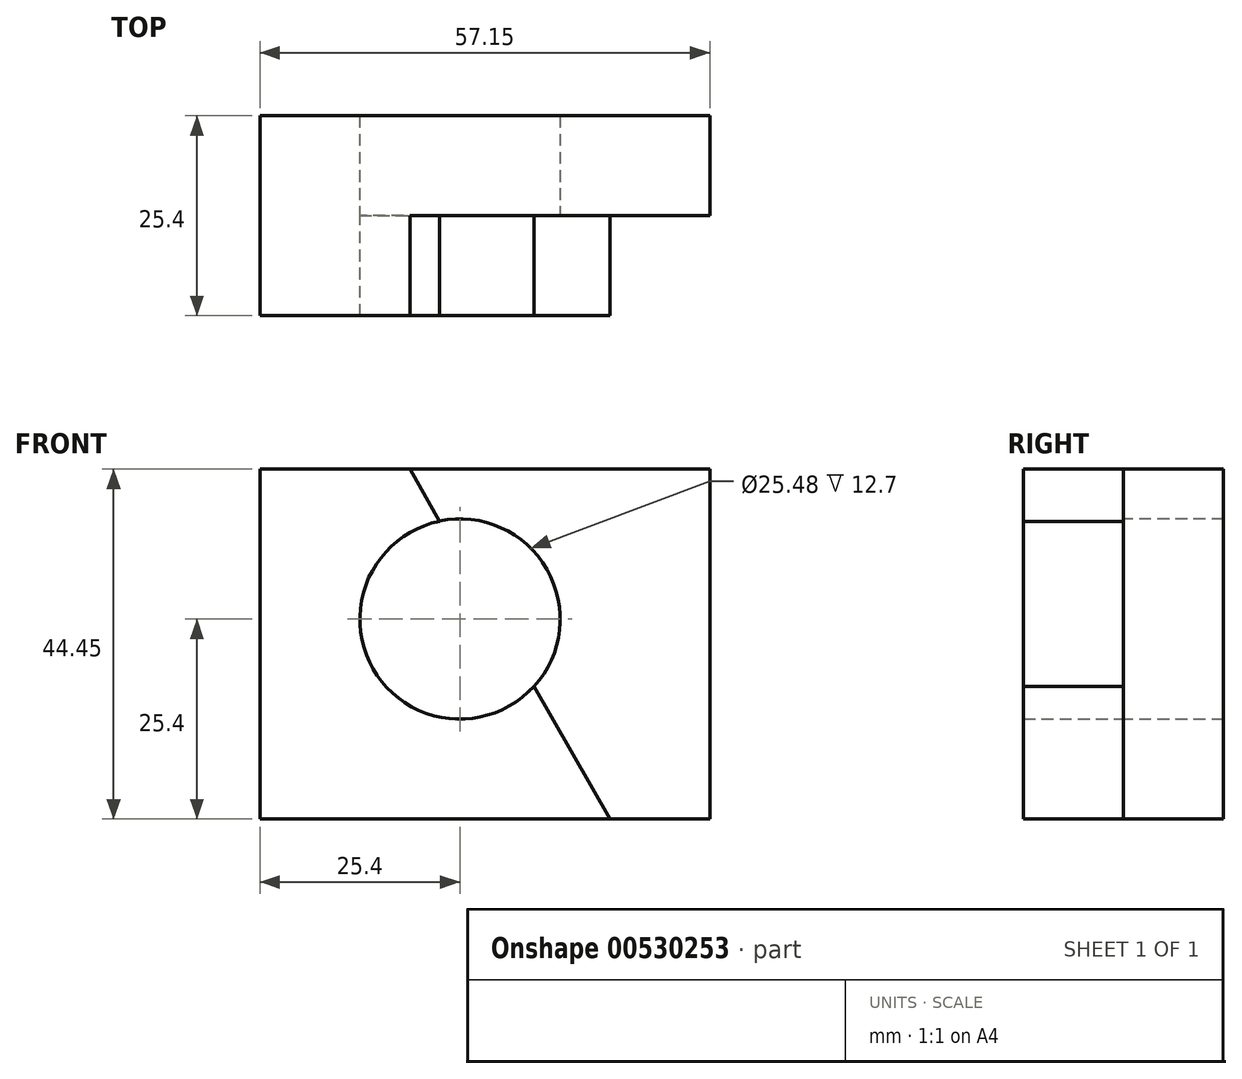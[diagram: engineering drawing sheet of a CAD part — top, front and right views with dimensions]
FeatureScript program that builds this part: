
annotation { "Feature Type Name" : "Feature", "Feature Type Description" : "" }
export const myFeature = defineFeature(function(context is Context, id is Id, definition is map)
    precondition{}
    {
        {
            var Q0;
            Q0=qCreatedBy(makeId("Front.planeOp"),FACE);
            var sketch = newSketch(context, id + "F0", { "sketchPlane" : qUnion([Q0])});
            skLineSegment(sketch, "E0.bottom", {"start": v(-57.15, 44.45) * mm, "end": v(0, 44.45) * mm});
            skLineSegment(sketch, "E0.top", {"start": v(-57.15, 0) * mm, "end": v(0, 0) * mm});
            skLineSegment(sketch, "E0.left", {"start": v(-57.15, 44.45) * mm, "end": v(-57.15, 0) * mm});
            skLineSegment(sketch, "E0.right", {"start": v(0, 44.45) * mm, "end": v(0, 0) * mm});
            skSolve(sketch);
        }
        {
            var Q0;
            Q0 = qSketchRegion(id + "F0", true);
            extrude(context, id + "F1", {"entities" : qUnion([Q0]), "depth" : 25.4 * mm, "offsetDistance" : 25.4 * mm});
        }
        {
            var Q0;
            Q0=makeQuery(id+"F1.opExtrude","CAP_FACE",FACE,{"disambiguationData":[OSD([sQuery(id+"F0.wireOp",EDGE,"E0.bottom"),sQuery(id+"F0.wireOp",EDGE,"E0.top"),sQuery(id+"F0.wireOp",EDGE,"E0.left"),sQuery(id+"F0.wireOp",EDGE,"E0.right")])],"isStart":false});
            var sketch = newSketch(context, id + "F2", { "sketchPlane" : qUnion([Q0])});
            skLineSegment(sketch, "E1", {"start": v(-38.1, 44.45) * mm, "end": v(-12.7, 0) * mm});
            skLineSegment(sketch, "E2", {"start": v(-12.7, 0) * mm, "end": v(0, 0) * mm});
            skLineSegment(sketch, "E3", {"start": v(0, 0) * mm, "end": v(0, 44.45) * mm});
            skLineSegment(sketch, "E4", {"start": v(0, 44.45) * mm, "end": v(-38.1, 44.45) * mm});
            skSolve(sketch);
        }
        {
            var Q0;
            Q0=makeQuery(id+"F2.imprint","IMPRINT",FACE,{"disambiguationData":[TD([[makeQuery(id+"F2.imprint","IMPRINT",EDGE,{"derivedFrom":sQuery(id+"F2.wireOp",EDGE,"E1")}),1.0]])]});
            extrude(context, id + "F3", {"entities" : qUnion([Q0]), "operationType" : NewBodyOperationType.REMOVE, "oppositeDirection" : true, "depth" : 12.7 * mm, "offsetDistance" : 25.4 * mm});
        }
        {
            var Q0;
            Q0=makeQuery(id+"F3.boolean.opBoolean","COPY",FACE,{"derivedFrom":makeQuery(id+"F3.opExtrude","CAP_FACE",FACE,{"disambiguationData":[OSD([sQuery(id+"F2.wireOp",EDGE,"E1"),sQuery(id+"F2.wireOp",EDGE,"E2"),sQuery(id+"F2.wireOp",EDGE,"E3"),sQuery(id+"F2.wireOp",EDGE,"E4")])],"isStart":false})});
            var sketch = newSketch(context, id + "F4", { "sketchPlane" : qUnion([Q0])});
            skCircle(sketch, "E5", {"center": v(-31.75, 25.4) * mm, "radius": 12.7 * mm});
            skSolve(sketch);
        }
        {
            var Q0;
            Q0 = qSketchRegion(id + "F4", true);
            extrude(context, id + "F5", {"entities" : qUnion([Q0]), "operationType" : NewBodyOperationType.REMOVE, "endBound" : BoundingType.THROUGH_ALL, "depth" : 25.4 * mm, "offsetDistance" : 25.4 * mm});
        }
        {
            var Q0;
            Q0=makeQuery(id+"F5.boolean.opBoolean","MERGE",FACE,{"derivedFrom":[makeQuery(id+"F3.boolean.opBoolean","COPY",FACE,{"derivedFrom":makeQuery(id+"F3.opExtrude","CAP_FACE",FACE,{"disambiguationData":[OSD([sQuery(id+"F2.wireOp",EDGE,"E1"),sQuery(id+"F2.wireOp",EDGE,"E2"),sQuery(id+"F2.wireOp",EDGE,"E3"),sQuery(id+"F2.wireOp",EDGE,"E4")])],"isStart":false})}),makeQuery(id+"F5.opExtrude","CAP_FACE",FACE,{"disambiguationData":[OSD([sQuery(id+"F4.wireOp",EDGE,"E5")])],"isStart":true})]});
            var sketch = newSketch(context, id + "F6", { "sketchPlane" : qUnion([Q0])});
            skCircle(sketch, "E6", {"center": v(-31.75, 25.4) * mm, "radius": 12.74 * mm});
            skSolve(sketch);
        }
        {
            var Q0;
            {var subQ1=sQuery(id+"F4.wireOp",EDGE,"E5");var subQ12=makeQuery(id+"F5.boolean.opBoolean","COPY",EDGE,{"derivedFrom":makeQuery(id+"F5.opExtrude","CAP_EDGE",EDGE,{"disambiguationData":[OSD([subQ1])],"isStart":true})});Q0=makeQuery(id+"F6.imprint","IMPRINT",FACE,{"disambiguationData":[TD([[makeQuery(id+"F6.imprint","IMPRINT",EDGE,{"derivedFrom":subQ12}),-1.0]])]});}
            var Q1;
            {var subQ1=sQuery(id+"F4.wireOp",EDGE,"E5");var subQ12=makeQuery(id+"F5.boolean.opBoolean","COPY",EDGE,{"derivedFrom":makeQuery(id+"F5.opExtrude","CAP_EDGE",EDGE,{"disambiguationData":[OSD([subQ1])],"isStart":true})});Q1=makeQuery(id+"F6.imprint","IMPRINT",FACE,{"disambiguationData":[TD([[makeQuery(id+"F6.imprint","IMPRINT",EDGE,{"derivedFrom":subQ12}),1.0]])]});}
            extrude(context, id + "F7", {"entities" : qUnion([Q0, Q1]), "operationType" : NewBodyOperationType.REMOVE, "oppositeDirection" : true, "depth" : 25.4 * mm, "offsetDistance" : 25.4 * mm});
        }
    });
